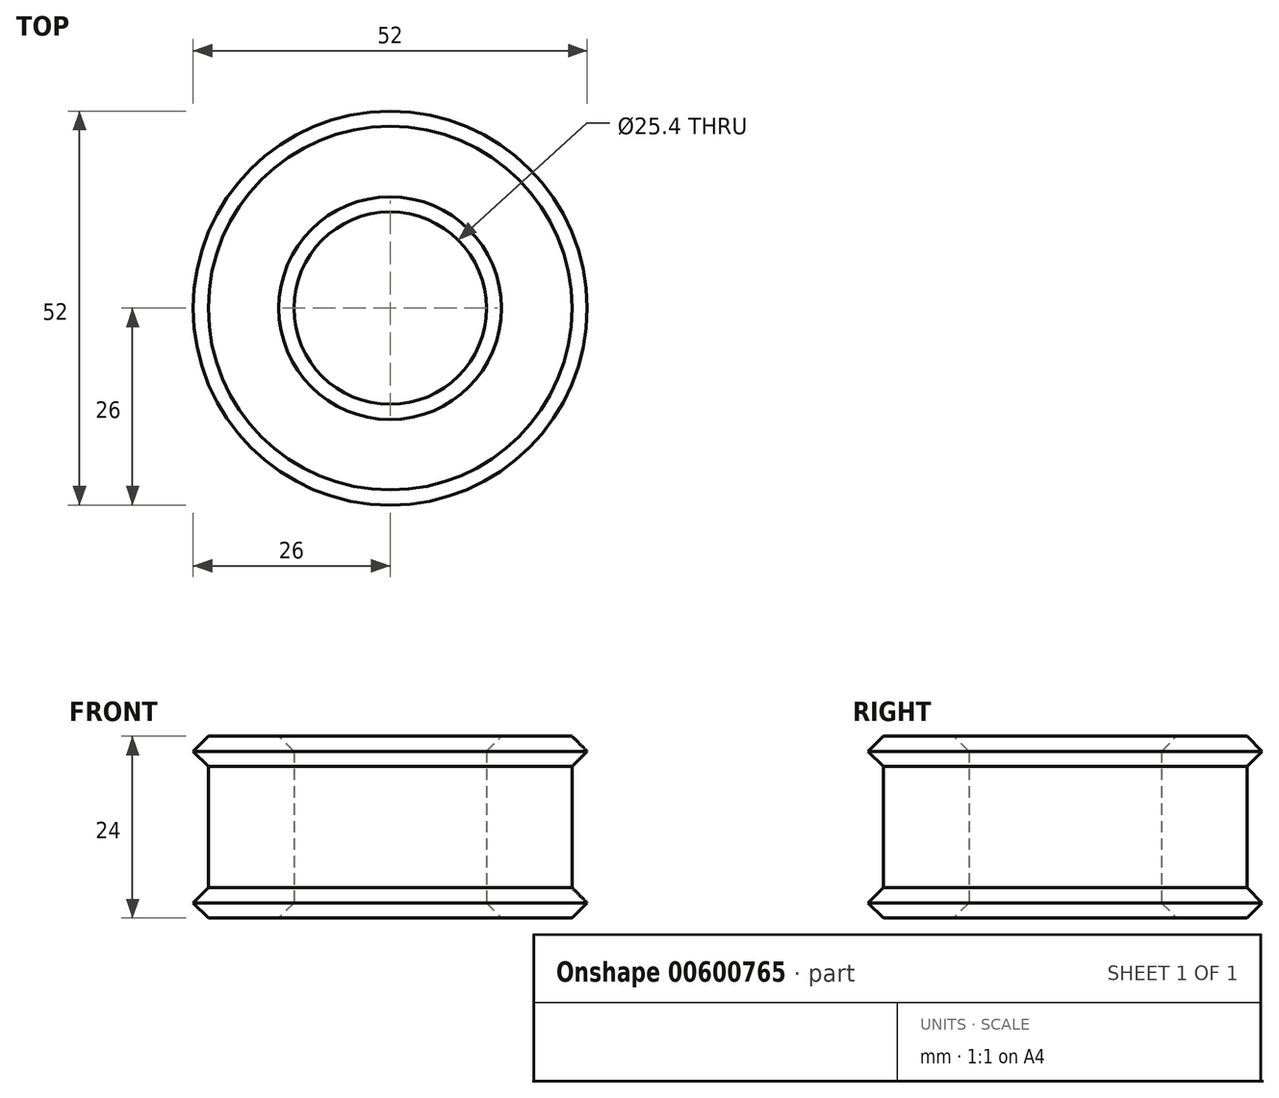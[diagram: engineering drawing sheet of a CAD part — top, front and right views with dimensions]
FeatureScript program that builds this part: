
annotation { "Feature Type Name" : "Feature", "Feature Type Description" : "" }
export const myFeature = defineFeature(function(context is Context, id is Id, definition is map)
    precondition{}
    {
        {
            var Q0;
            Q0=qCreatedBy(makeId("Top.planeOp"),FACE);
            var sketch = newSketch(context, id + "F0", { "sketchPlane" : qUnion([Q0])});
            skCircle(sketch, "E0", {"center": v(0, 0) * mm, "radius": 12.7 * mm});
            skCircle(sketch, "E1", {"center": v(0, 0) * mm, "radius": 26 * mm});
            skCircle(sketch, "E2", {"center": v(0, 0) * mm, "radius": 24 * mm});
            skSolve(sketch);
        }
        {
            var Q0;
            Q0=makeQuery(id+"F0.imprint","IMPRINT",FACE,{"disambiguationData":[TD([[makeQuery(id+"F0.imprint","IMPRINT",EDGE,{"derivedFrom":sQuery(id+"F0.wireOp",EDGE,"E0")}),-1.0]])]});
            extrude(context, id + "F1", {"entities" : qUnion([Q0]), "depth" : 24 * mm, "offsetDistance" : 25 * mm});
        }
        {
            var Q0;
            Q0=makeQuery(id+"F0.imprint","IMPRINT",FACE,{"disambiguationData":[TD([[makeQuery(id+"F0.imprint","IMPRINT",EDGE,{"derivedFrom":sQuery(id+"F0.wireOp",EDGE,"E1")}),1.0]])]});
            extrude(context, id + "F2", {"entities" : qUnion([Q0]), "operationType" : NewBodyOperationType.ADD, "depth" : 4 * mm, "offsetDistance" : 25 * mm});
        }
        {
            var Q0;
            Q0=makeQuery(id+"F0.imprint","IMPRINT",FACE,{"disambiguationData":[TD([[makeQuery(id+"F0.imprint","IMPRINT",EDGE,{"derivedFrom":sQuery(id+"F0.wireOp",EDGE,"E1")}),1.0]])]});
            extrude(context, id + "F3", {"entities" : qUnion([Q0]), "operationType" : NewBodyOperationType.ADD, "depth" : 24 * mm, "offsetDistance" : 25 * mm, "hasSecondDirection" : true, "secondDirectionOppositeDirection" : false, "secondDirectionDepth" : 20 * mm});
        }
        {
            var Q0;
            Q0=makeQuery(id+"F3.opExtrude","CAP_EDGE",EDGE,{"disambiguationData":[OSD([sQuery(id+"F0.wireOp",EDGE,"E1")])],"isStart":true});
            var Q1;
            Q1=makeQuery(id+"F3.opExtrude","CAP_EDGE",EDGE,{"disambiguationData":[OSD([sQuery(id+"F0.wireOp",EDGE,"E1")])],"isStart":false});
            var Q2;
            Q2=makeQuery(id+"F2.opExtrude","CAP_EDGE",EDGE,{"disambiguationData":[OSD([sQuery(id+"F0.wireOp",EDGE,"E1")])],"isStart":false});
            var Q3;
            Q3=makeQuery(id+"F2.opExtrude","CAP_EDGE",EDGE,{"disambiguationData":[OSD([sQuery(id+"F0.wireOp",EDGE,"E1")])],"isStart":true});
            var Q4;
            Q4=makeQuery(id+"F1.opExtrude","CAP_EDGE",EDGE,{"disambiguationData":[OSD([sQuery(id+"F0.wireOp",EDGE,"E0")])],"isStart":true});
            var Q5;
            Q5=makeQuery(id+"F1.opExtrude","SWEPT_FACE",FACE,{"disambiguationData":[OSD([sQuery(id+"F0.wireOp",EDGE,"E0")])]});
            chamfer(context, id + "F4", {"entities" : qUnion([Q0, Q1, Q2, Q3, Q4, Q5]), "width" : 2 * mm, "tangentPropagation" : true});
        }
    });
